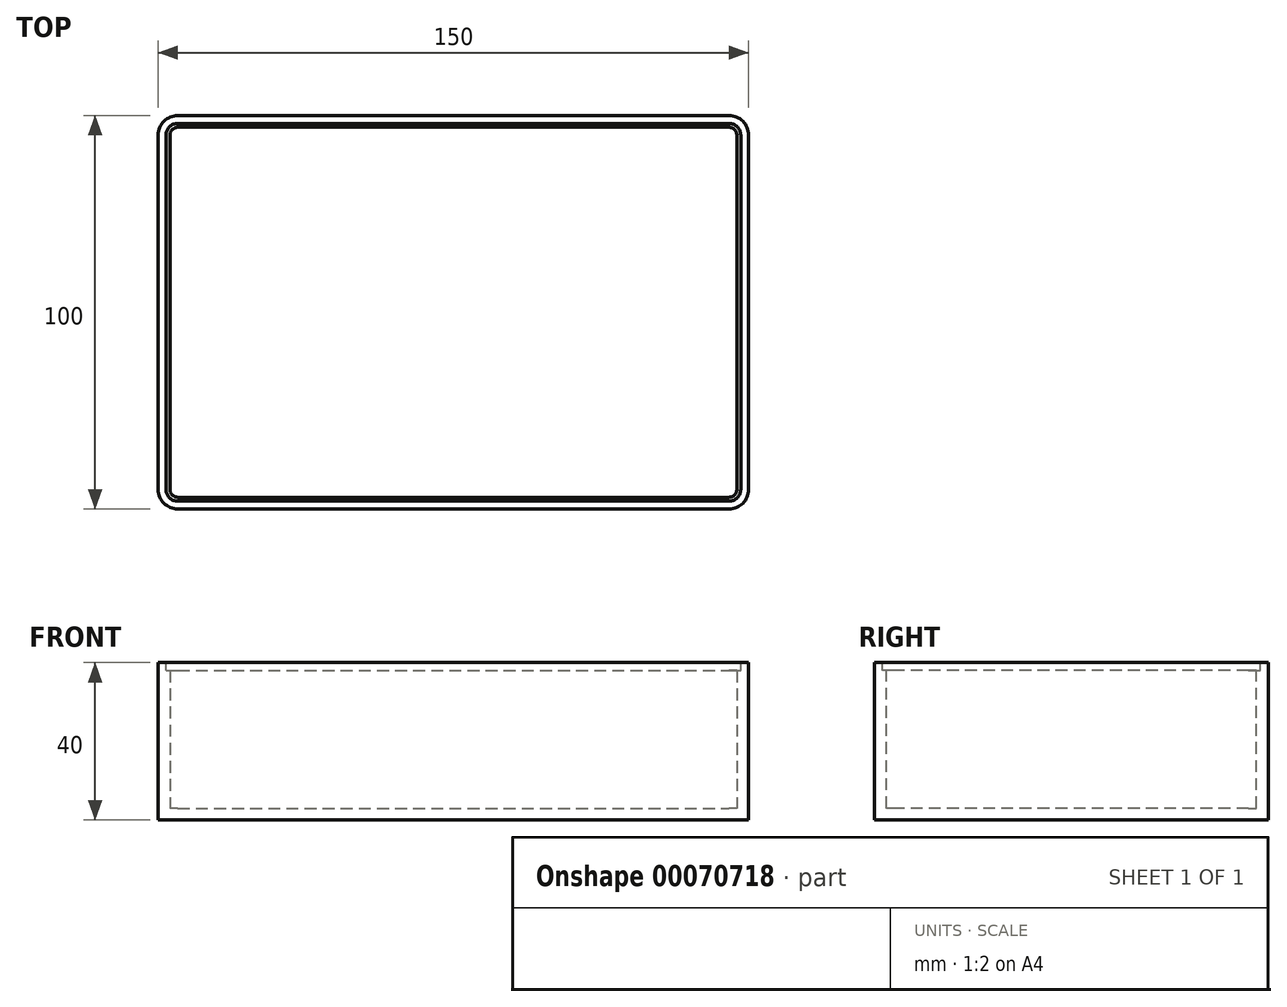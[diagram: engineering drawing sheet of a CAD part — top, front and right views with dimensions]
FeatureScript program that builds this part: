
annotation { "Feature Type Name" : "Feature", "Feature Type Description" : "" }
export const myFeature = defineFeature(function(context is Context, id is Id, definition is map)
    precondition{}
    {
        {
            var Q0;
            Q0=qCreatedBy(makeId("Top.planeOp"),FACE);
            var sketch = newSketch(context, id + "F0", { "sketchPlane" : qUnion([Q0])});
            skLineSegment(sketch, "E0.rect.bottom", {"start": v(-75, 50) * mm, "end": v(75, 50) * mm});
            skLineSegment(sketch, "E0.rect.top", {"start": v(-75, -50) * mm, "end": v(75, -50) * mm});
            skLineSegment(sketch, "E0.rect.left", {"start": v(-75, 50) * mm, "end": v(-75, -50) * mm});
            skLineSegment(sketch, "E0.rect.right", {"start": v(75, 50) * mm, "end": v(75, -50) * mm});
            skPoint(sketch, "E0.rect.middle", {"position": v(0, 0) * mm});
            skSolve(sketch);
        }
        {
            var Q0;
            Q0=makeQuery(id+"F0.imprint","IMPRINT",FACE,{"disambiguationData":[TD([[makeQuery(id+"F0.imprint","IMPRINT",EDGE,{"derivedFrom":sQuery(id+"F0.wireOp",EDGE,"E0.rect.bottom")}),-1.0]])]});
            extrude(context, id + "F1", {"entities" : qUnion([Q0]), "depth" : 40 * mm});
        }
        {
            var Q0;
            Q0=makeQuery(id+"F1.opExtrude","SWEPT_EDGE",EDGE,{"disambiguationData":[OSD([sQuery(id+"F0.wireOp",EDGE,"E0.rect.bottom"),sQuery(id+"F0.wireOp",EDGE,"E0.rect.right")])]});
            var Q1;
            Q1=makeQuery(id+"F1.opExtrude","SWEPT_EDGE",EDGE,{"disambiguationData":[OSD([sQuery(id+"F0.wireOp",EDGE,"E0.rect.bottom"),sQuery(id+"F0.wireOp",EDGE,"E0.rect.left")])]});
            var Q2;
            Q2=makeQuery(id+"F1.opExtrude","SWEPT_EDGE",EDGE,{"disambiguationData":[OSD([sQuery(id+"F0.wireOp",EDGE,"E0.rect.top"),sQuery(id+"F0.wireOp",EDGE,"E0.rect.left")])]});
            var Q3;
            Q3=makeQuery(id+"F1.opExtrude","SWEPT_EDGE",EDGE,{"disambiguationData":[OSD([sQuery(id+"F0.wireOp",EDGE,"E0.rect.top"),sQuery(id+"F0.wireOp",EDGE,"E0.rect.right")])]});
            fillet(context, id + "F2", {"entities" : qUnion([Q0, Q1, Q2, Q3]), "radius" : 5 * mm, "tangentPropagation" : true, "allowEdgeOverflow" : false});
        }
        {
            var Q0;
            Q0=makeQuery(id+"F1.opExtrude","CAP_FACE",FACE,{"disambiguationData":[OSD([sQuery(id+"F0.wireOp",EDGE,"E0.rect.bottom"),sQuery(id+"F0.wireOp",EDGE,"E0.rect.top"),sQuery(id+"F0.wireOp",EDGE,"E0.rect.left"),sQuery(id+"F0.wireOp",EDGE,"E0.rect.right")])],"isStart":false});
            shell(context, id + "F3", {"entities" : qUnion([Q0]), "thickness" : 3 * mm});
        }
        {
            var Q0;
            Q0=makeQuery(id+"F1.opExtrude","CAP_FACE",FACE,{"disambiguationData":[OSD([sQuery(id+"F0.wireOp",EDGE,"E0.rect.bottom"),sQuery(id+"F0.wireOp",EDGE,"E0.rect.top"),sQuery(id+"F0.wireOp",EDGE,"E0.rect.left"),sQuery(id+"F0.wireOp",EDGE,"E0.rect.right")])],"isStart":false});
            var sketch = newSketch(context, id + "F4", { "sketchPlane" : qUnion([Q0])});
            skLineSegment(sketch, "E1.rect.bottom", {"start": v(-73, 48) * mm, "end": v(73, 48) * mm});
            skLineSegment(sketch, "E1.rect.top", {"start": v(-73, -48) * mm, "end": v(73, -48) * mm});
            skLineSegment(sketch, "E1.rect.left", {"start": v(-73, 48) * mm, "end": v(-73, -48) * mm});
            skLineSegment(sketch, "E1.rect.right", {"start": v(73, 48) * mm, "end": v(73, -48) * mm});
            skPoint(sketch, "E1.rect.middle", {"position": v(0, 0) * mm});
            skSolve(sketch);
        }
        {
            var Q0;
            Q0 = qSketchRegion(id + "F4", true);
            extrude(context, id + "F5", {"entities" : qUnion([Q0]), "operationType" : NewBodyOperationType.REMOVE, "oppositeDirection" : true, "depth" : 2 * mm});
        }
        {
            var Q0;
            Q0=makeQuery(id+"F5.boolean.opBoolean","COPY",EDGE,{"derivedFrom":makeQuery(id+"F5.opExtrude","SWEPT_EDGE",EDGE,{"disambiguationData":[OSD([sQuery(id+"F4.wireOp",EDGE,"E1.rect.bottom"),sQuery(id+"F4.wireOp",EDGE,"E1.rect.right")])]})});
            var Q1;
            Q1=makeQuery(id+"F5.boolean.opBoolean","COPY",EDGE,{"derivedFrom":makeQuery(id+"F5.opExtrude","SWEPT_EDGE",EDGE,{"disambiguationData":[OSD([sQuery(id+"F4.wireOp",EDGE,"E1.rect.top"),sQuery(id+"F4.wireOp",EDGE,"E1.rect.right")])]})});
            var Q2;
            Q2=makeQuery(id+"F5.boolean.opBoolean","COPY",EDGE,{"derivedFrom":makeQuery(id+"F5.opExtrude","SWEPT_EDGE",EDGE,{"disambiguationData":[OSD([sQuery(id+"F4.wireOp",EDGE,"E1.rect.bottom"),sQuery(id+"F4.wireOp",EDGE,"E1.rect.left")])]})});
            var Q3;
            Q3=makeQuery(id+"F5.boolean.opBoolean","COPY",EDGE,{"derivedFrom":makeQuery(id+"F5.opExtrude","SWEPT_EDGE",EDGE,{"disambiguationData":[OSD([sQuery(id+"F4.wireOp",EDGE,"E1.rect.top"),sQuery(id+"F4.wireOp",EDGE,"E1.rect.left")])]})});
            fillet(context, id + "F6", {"entities" : qUnion([Q0, Q1, Q2, Q3]), "radius" : 3 * mm, "tangentPropagation" : true, "allowEdgeOverflow" : false});
        }
    });
